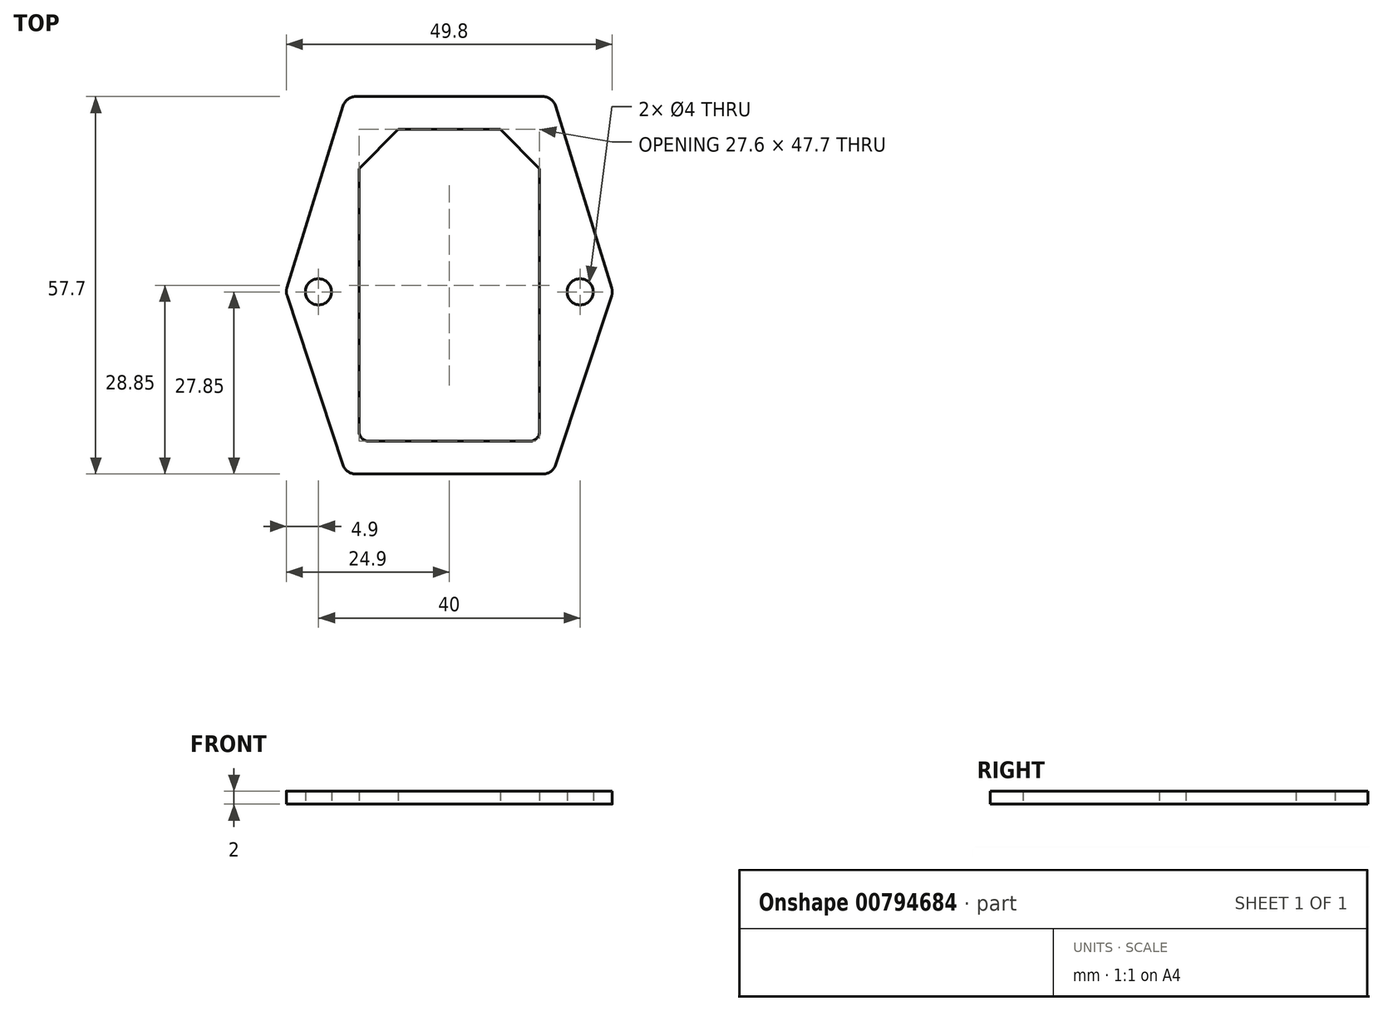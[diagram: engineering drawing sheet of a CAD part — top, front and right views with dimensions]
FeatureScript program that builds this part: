
annotation { "Feature Type Name" : "Feature", "Feature Type Description" : "" }
export const myFeature = defineFeature(function(context is Context, id is Id, definition is map)
    precondition{}
    {
        {
            var Q0;
            Q0=qCreatedBy(makeId("Top.planeOp"),FACE);
            var sketch = newSketch(context, id + "F0", { "sketchPlane" : qUnion([Q0])});
            skLineSegment(sketch, "E0.bottom", {"start": v(15.8, 28.85) * mm, "end": v(-15.8, 28.85) * mm});
            skLineSegment(sketch, "E0.top", {"start": v(15.8, -28.85) * mm, "end": v(-15.8, -28.85) * mm});
            skLineSegment(sketch, "E0.left", {"start": v(15.8, 28.85) * mm, "end": v(15.8, -28.85) * mm});
            skLineSegment(sketch, "E0.right", {"start": v(-15.8, 28.85) * mm, "end": v(-15.8, -28.85) * mm});
            skPoint(sketch, "E0.middle", {"position": v(0, 0) * mm});
            skLineSegment(sketch, "E1.bottom", {"start": v(13.8, 23.85) * mm, "end": v(-13.8, 23.85) * mm});
            skLineSegment(sketch, "E1.top", {"start": v(13.8, -23.85) * mm, "end": v(-13.8, -23.85) * mm});
            skLineSegment(sketch, "E1.left", {"start": v(13.8, 23.85) * mm, "end": v(13.8, -23.85) * mm});
            skLineSegment(sketch, "E1.right", {"start": v(-13.8, 23.85) * mm, "end": v(-13.8, -23.85) * mm});
            skLineSegment(sketch, "E2", {"start": v(-13.8, 17.85) * mm, "end": v(-7.8, 23.85) * mm});
            skLineSegment(sketch, "E3.MirrorCS", {"start": v(13.8, 17.85) * mm, "end": v(7.8, 23.85) * mm});
            skCircle(sketch, "E4", {"center": v(-20, -1) * mm, "radius": 2 * mm});
            skCircle(sketch, "E5.MirrorC", {"center": v(20, -1) * mm, "radius": 2 * mm});
            skLineSegment(sketch, "E6", {"start": v(-15.8, 28.85) * mm, "end": v(-25, -1) * mm});
            skLineSegment(sketch, "E7", {"start": v(-25, -1) * mm, "end": v(-15.8, -28.85) * mm});
            skLineSegment(sketch, "E8.MirrorCS", {"start": v(15.8, 28.85) * mm, "end": v(25, -1) * mm});
            skLineSegment(sketch, "E9.MirrorCS", {"start": v(25, -1) * mm, "end": v(15.8, -28.85) * mm});
            skSolve(sketch);
        }
        {
            var Q0;
            {var subQ3=sQuery(id+"F0.wireOp",EDGE,"E2");Q0=makeQuery(id+"F0.imprint","IMPRINT",FACE,{"disambiguationData":[TD([[makeQuery(id+"F0.imprint","IMPRINT",EDGE,{"derivedFrom":subQ3}),1.0]])]});}
            var Q1;
            {var subQ13=sQuery(id+"F0.wireOp",EDGE,"E0.bottom");Q1=makeQuery(id+"F0.imprint","IMPRINT",FACE,{"disambiguationData":[TD([[makeQuery(id+"F0.imprint","IMPRINT",EDGE,{"derivedFrom":subQ13}),1.0]])]});}
            var Q2;
            {var subQ3=sQuery(id+"F0.wireOp",EDGE,"E3.MirrorCS");Q2=makeQuery(id+"F0.imprint","IMPRINT",FACE,{"disambiguationData":[TD([[makeQuery(id+"F0.imprint","IMPRINT",EDGE,{"derivedFrom":subQ3}),-1.0]])]});}
            var Q3;
            {var subQ4=sQuery(id+"F0.wireOp",EDGE,"56c1c3bb-a0c1-44e5-9ecd-d2cbaad9352f0.MirrorCS");Q3=makeQuery(id+"F0.imprint","IMPRINT",FACE,{"disambiguationData":[TD([[makeQuery(id+"F0.imprint","IMPRINT",EDGE,{"derivedFrom":subQ4}),-1.0]])]});}
            var Q4;
            {var subQ5=sQuery(id+"F0.wireOp",EDGE,"kKEwGwVK-5YBT-lCU5-zwI2-KIaJYYhc4CLR");Q4=makeQuery(id+"F0.imprint","IMPRINT",FACE,{"disambiguationData":[TD([[makeQuery(id+"F0.imprint","IMPRINT",EDGE,{"derivedFrom":subQ5}),1.0]])]});}
            var Q5;
            Q5=makeQuery(id+"F0.imprint","IMPRINT",FACE,{"disambiguationData":[TD([[makeQuery(id+"F0.imprint","IMPRINT",EDGE,{"derivedFrom":sQuery(id+"F0.wireOp",EDGE,"E0.right")}),-1.0]])]});
            var Q6;
            Q6=makeQuery(id+"F0.imprint","IMPRINT",FACE,{"disambiguationData":[TD([[makeQuery(id+"F0.imprint","IMPRINT",EDGE,{"derivedFrom":sQuery(id+"F0.wireOp",EDGE,"E0.left")}),1.0]])]});
            extrude(context, id + "F1", {"entities" : qUnion([Q0, Q1, Q2, Q3, Q4, Q5, Q6]), "depth" : 2 * mm, "offsetDistance" : 25 * mm});
        }
        {
            var Q0;
            Q0=makeQuery(id+"F1.opExtrude","SWEPT_EDGE",EDGE,{"disambiguationData":[OSD([sQuery(id+"F0.wireOp",EDGE,"E1.top"),sQuery(id+"F0.wireOp",EDGE,"E1.left")])]});
            var Q1;
            Q1=makeQuery(id+"F1.opExtrude","SWEPT_EDGE",EDGE,{"disambiguationData":[OSD([sQuery(id+"F0.wireOp",EDGE,"E1.top"),sQuery(id+"F0.wireOp",EDGE,"E1.right")])]});
            fillet(context, id + "F2", {"entities" : qUnion([Q0, Q1]), "radius" : 1.5 * mm, "tangentPropagation" : true, "allowEdgeOverflow" : false});
        }
        {
            var Q0;
            Q0=makeQuery(id+"F1.opExtrude","SWEPT_EDGE",EDGE,{"disambiguationData":[OSD([sQuery(id+"F0.wireOp",EDGE,"E0.top"),sQuery(id+"F0.wireOp",EDGE,"E0.left"),sQuery(id+"F0.wireOp",EDGE,"E9.MirrorCS")])]});
            var Q1;
            Q1=makeQuery(id+"F1.opExtrude","SWEPT_EDGE",EDGE,{"disambiguationData":[OSD([sQuery(id+"F0.wireOp",EDGE,"E0.top"),sQuery(id+"F0.wireOp",EDGE,"E0.right"),sQuery(id+"F0.wireOp",EDGE,"E7")])]});
            var Q2;
            Q2=makeQuery(id+"F1.opExtrude","SWEPT_EDGE",EDGE,{"disambiguationData":[OSD([sQuery(id+"F0.wireOp",EDGE,"E8.MirrorCS"),sQuery(id+"F0.wireOp",EDGE,"E9.MirrorCS")])]});
            var Q3;
            Q3=makeQuery(id+"F1.opExtrude","SWEPT_EDGE",EDGE,{"disambiguationData":[OSD([sQuery(id+"F0.wireOp",EDGE,"E0.bottom"),sQuery(id+"F0.wireOp",EDGE,"E0.left"),sQuery(id+"F0.wireOp",EDGE,"E8.MirrorCS")])]});
            var Q4;
            Q4=makeQuery(id+"F1.opExtrude","SWEPT_EDGE",EDGE,{"disambiguationData":[OSD([sQuery(id+"F0.wireOp",EDGE,"E0.bottom"),sQuery(id+"F0.wireOp",EDGE,"E0.right"),sQuery(id+"F0.wireOp",EDGE,"E6")])]});
            var Q5;
            Q5=makeQuery(id+"F1.opExtrude","SWEPT_EDGE",EDGE,{"disambiguationData":[OSD([sQuery(id+"F0.wireOp",EDGE,"E6"),sQuery(id+"F0.wireOp",EDGE,"E7")])]});
            fillet(context, id + "F3", {"entities" : qUnion([Q0, Q1, Q2, Q3, Q4, Q5]), "radius" : 2 * mm, "tangentPropagation" : true, "allowEdgeOverflow" : false});
        }
    });
